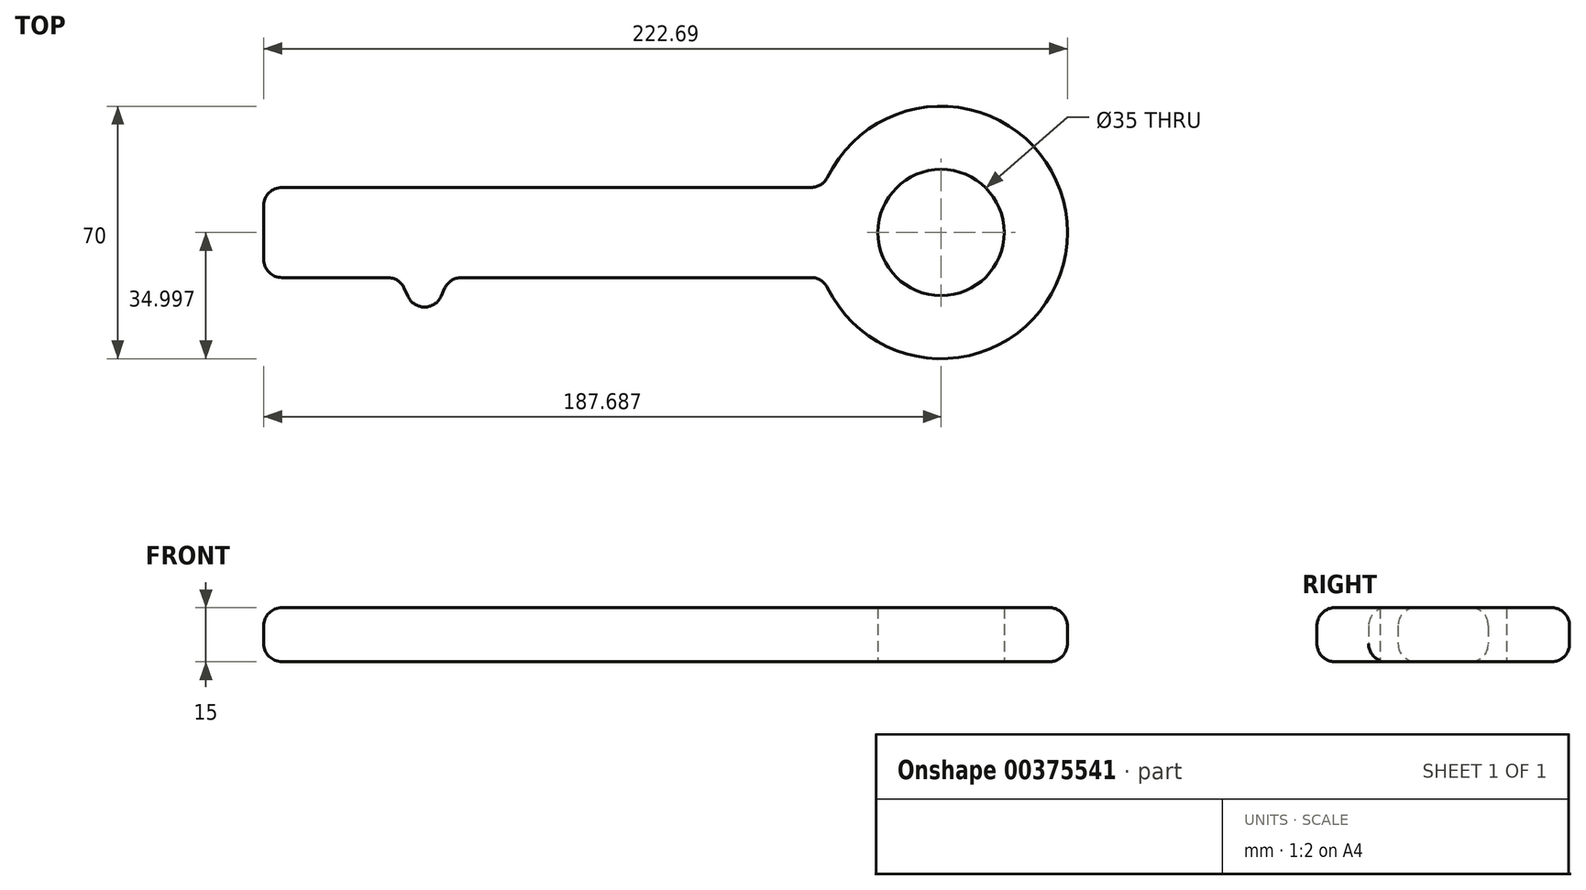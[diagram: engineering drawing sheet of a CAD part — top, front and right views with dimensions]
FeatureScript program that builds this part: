
annotation { "Feature Type Name" : "Feature", "Feature Type Description" : "" }
export const myFeature = defineFeature(function(context is Context, id is Id, definition is map)
    precondition{}
    {
        {
            var Q0;
            Q0=qCreatedBy(makeId("Top.planeOp"),FACE);
            var sketch = newSketch(context, id + "F0", { "sketchPlane" : qUnion([Q0])});
            skLineSegment(sketch, "E0.bottom", {"start": v(-91.14, 51.92) * mm, "end": v(63.86, 51.92) * mm});
            skLineSegment(sketch, "E0.top", {"start": v(-91.14, 26.92) * mm, "end": v(63.86, 26.92) * mm});
            skLineSegment(sketch, "E0.left", {"start": v(-91.14, 51.92) * mm, "end": v(-91.14, 26.92) * mm});
            skLineSegment(sketch, "E0.right", {"start": v(63.86, 51.92) * mm, "end": v(63.86, 26.92) * mm});
            skLineSegment(sketch, "E1.bottom", {"start": v(-91.14, 26.92) * mm, "end": v(-81.14, 26.92) * mm});
            skLineSegment(sketch, "E1.top", {"start": v(-91.14, -3.08) * mm, "end": v(-81.14, -3.08) * mm});
            skLineSegment(sketch, "E1.left", {"start": v(-91.14, 26.92) * mm, "end": v(-91.14, -3.08) * mm});
            skLineSegment(sketch, "E1.right", {"start": v(-81.14, 26.92) * mm, "end": v(-81.14, -3.08) * mm});
            skLineSegment(sketch, "E2.bottom", {"start": v(-71.14, 26.92) * mm, "end": v(-63.6, 26.92) * mm});
            skLineSegment(sketch, "E2.top", {"start": v(-71.14, 11.92) * mm, "end": v(-63.6, 11.92) * mm});
            skLineSegment(sketch, "E2.left", {"start": v(-71.14, 26.92) * mm, "end": v(-71.14, 11.92) * mm});
            skLineSegment(sketch, "E2.right", {"start": v(-63.6, 26.92) * mm, "end": v(-63.6, 11.92) * mm});
            skLineSegment(sketch, "E3", {"start": v(-53.6, 26.92) * mm, "end": v(-46.6, 11.92) * mm});
            skLineSegment(sketch, "E4", {"start": v(-46.6, 11.92) * mm, "end": v(-39.6, 26.92) * mm});
            skLineSegment(sketch, "E5", {"start": v(-39.6, 26.92) * mm, "end": v(-46.6, 26.92) * mm});
            skArc(sketch, "E6", {"start": v(63.86, 26.92) * mm, "mid": v(131.55, 39.42) * mm, "end": v(63.86, 51.92) * mm});
            skCircle(sketch, "E7", {"center": v(96.55, 39.42) * mm, "radius": 17.5 * mm});
            skSolve(sketch);
        }
        {
            var Q0;
            Q0=makeQuery(id+"F0.imprint","IMPRINT",FACE,{"disambiguationData":[TD([[makeQuery(id+"F0.imprint","IMPRINT",EDGE,{"derivedFrom":sQuery(id+"F0.wireOp",EDGE,"E0.bottom")}),-1.0]])]});
            var Q1;
            {var subQ0=sQuery(id+"F0.wireOp",EDGE,"E3");Q1=makeQuery(id+"F0.imprint","IMPRINT",FACE,{"disambiguationData":[TD([[makeQuery(id+"F0.imprint","IMPRINT",EDGE,{"derivedFrom":subQ0}),1.0]])]});}
            var Q2;
            Q2=makeQuery(id+"F0.imprint","IMPRINT",FACE,{"disambiguationData":[TD([[makeQuery(id+"F0.imprint","IMPRINT",EDGE,{"derivedFrom":sQuery(id+"F0.wireOp",EDGE,"E2.bottom")}),-1.0]])]});
            var Q3;
            Q3=makeQuery(id+"F0.imprint","IMPRINT",FACE,{"disambiguationData":[TD([[makeQuery(id+"F0.imprint","IMPRINT",EDGE,{"derivedFrom":sQuery(id+"F0.wireOp",EDGE,"E1.bottom")}),-1.0]])]});
            var Q4;
            Q4=makeQuery(id+"F0.imprint","IMPRINT",FACE,{"disambiguationData":[TD([[makeQuery(id+"F0.imprint","IMPRINT",EDGE,{"derivedFrom":sQuery(id+"F0.wireOp",EDGE,"E0.right")}),1.0]])]});
            extrude(context, id + "F1", {"entities" : qUnion([Q0, Q1, Q2, Q3, Q4]), "depth" : 15 * mm});
        }
        {
            var Q0;
            Q0=makeQuery(id+"F1.opExtrude","CAP_EDGE",EDGE,{"disambiguationData":[OSD([sQuery(id+"F0.wireOp",EDGE,"E0.bottom")])],"isStart":false});
            var Q1;
            Q1=makeQuery(id+"F1.opExtrude","CAP_EDGE",EDGE,{"disambiguationData":[OSD([sQuery(id+"F0.wireOp",EDGE,"E0.left"),sQuery(id+"F0.wireOp",EDGE,"E1.left")])],"isStart":false});
            var Q2;
            Q2=makeQuery(id+"F1.opExtrude","CAP_EDGE",EDGE,{"disambiguationData":[OSD([sQuery(id+"F0.wireOp",EDGE,"E1.right")])],"isStart":false});
            var Q3;
            Q3=makeQuery(id+"F1.opExtrude","CAP_EDGE",EDGE,{"disambiguationData":[OSD([sQuery(id+"F0.wireOp",EDGE,"E1.top")])],"isStart":false});
            var Q4;
            Q4=makeQuery(id+"F1.opExtrude","CAP_EDGE",EDGE,{"disambiguationData":[OSD([sQuery(id+"F0.wireOp",EDGE,"E2.left")])],"isStart":false});
            var Q5;
            {var subQ0=sQuery(id+"F0.wireOp",EDGE,"E0.top");Q5=makeQuery(id+"F1.opExtrude","CAP_EDGE",EDGE,{"disambiguationData":[OSD([subQ0]),TDD([makeQuery(id+"F0.imprint","IMPRINT",EDGE,{"disambiguationData":[TD([[makeQuery(id+"F0.imprint","INTERSECT",VERTEX,{"derivedFrom":[subQ0,sQuery(id+"F0.wireOp",EDGE,"E3")]}),1.0]])],"derivedFrom":subQ0})])],"isStart":false});}
            var Q6;
            Q6=makeQuery(id+"F1.opExtrude","CAP_EDGE",EDGE,{"disambiguationData":[OSD([sQuery(id+"F0.wireOp",EDGE,"E2.right")])],"isStart":false});
            var Q7;
            Q7=makeQuery(id+"F1.opExtrude","CAP_EDGE",EDGE,{"disambiguationData":[OSD([sQuery(id+"F0.wireOp",EDGE,"E3")])],"isStart":false});
            var Q8;
            Q8=makeQuery(id+"F1.opExtrude","CAP_EDGE",EDGE,{"disambiguationData":[OSD([sQuery(id+"F0.wireOp",EDGE,"E2.top")])],"isStart":false});
            var Q9;
            Q9=makeQuery(id+"F1.opExtrude","CAP_EDGE",EDGE,{"disambiguationData":[OSD([sQuery(id+"F0.wireOp",EDGE,"E4")])],"isStart":false});
            var Q10;
            {var subQ0=sQuery(id+"F0.wireOp",EDGE,"E0.top");Q10=makeQuery(id+"F1.opExtrude","CAP_EDGE",EDGE,{"disambiguationData":[OSD([subQ0]),TDD([makeQuery(id+"F0.imprint","IMPRINT",EDGE,{"disambiguationData":[TD([[makeQuery(id+"F0.imprint","INTERSECT",VERTEX,{"derivedFrom":[subQ0,sQuery(id+"F0.wireOp",EDGE,"E0.right"),sQuery(id+"F0.wireOp",EDGE,"E6")]}),1.0]])],"derivedFrom":subQ0})])],"isStart":false});}
            var Q11;
            {var subQ0=sQuery(id+"F0.wireOp",EDGE,"E0.top");Q11=makeQuery(id+"F1.opExtrude","CAP_EDGE",EDGE,{"disambiguationData":[OSD([subQ0]),TDD([makeQuery(id+"F0.imprint","IMPRINT",EDGE,{"disambiguationData":[TD([[makeQuery(id+"F0.imprint","INTERSECT",VERTEX,{"derivedFrom":[subQ0,sQuery(id+"F0.wireOp",EDGE,"E1.bottom"),sQuery(id+"F0.wireOp",EDGE,"E1.right")]}),-1.0]])],"derivedFrom":subQ0})])],"isStart":false});}
            var Q12;
            Q12=makeQuery(id+"F1.opExtrude","CAP_EDGE",EDGE,{"disambiguationData":[OSD([sQuery(id+"F0.wireOp",EDGE,"E0.left"),sQuery(id+"F0.wireOp",EDGE,"E1.left")])],"isStart":true});
            var Q13;
            Q13=makeQuery(id+"F1.opExtrude","SWEPT_EDGE",EDGE,{"disambiguationData":[OSD([sQuery(id+"F0.wireOp",EDGE,"E0.bottom"),sQuery(id+"F0.wireOp",EDGE,"E0.left")])]});
            var Q14;
            Q14=makeQuery(id+"F1.opExtrude","CAP_EDGE",EDGE,{"disambiguationData":[OSD([sQuery(id+"F0.wireOp",EDGE,"E6")])],"isStart":false});
            var Q15;
            Q15=makeQuery(id+"F1.opExtrude","CAP_EDGE",EDGE,{"disambiguationData":[OSD([sQuery(id+"F0.wireOp",EDGE,"E6")])],"isStart":true});
            var Q16;
            Q16=makeQuery(id+"F1.opExtrude","SWEPT_FACE",FACE,{"disambiguationData":[OSD([sQuery(id+"F0.wireOp",EDGE,"E6")])]});
            var Q17;
            Q17=makeQuery(id+"F1.opExtrude","SWEPT_EDGE",EDGE,{"disambiguationData":[OSD([sQuery(id+"F0.wireOp",EDGE,"E1.top"),sQuery(id+"F0.wireOp",EDGE,"E1.left")])]});
            var Q18;
            {var subQ0=sQuery(id+"F0.wireOp",EDGE,"E0.top");Q18=makeQuery(id+"F1.opExtrude","CAP_EDGE",EDGE,{"disambiguationData":[OSD([subQ0]),TDD([makeQuery(id+"F0.imprint","IMPRINT",EDGE,{"disambiguationData":[TD([[makeQuery(id+"F0.imprint","INTERSECT",VERTEX,{"derivedFrom":[subQ0,sQuery(id+"F0.wireOp",EDGE,"E0.right"),sQuery(id+"F0.wireOp",EDGE,"E6")]}),1.0]])],"derivedFrom":subQ0})])],"isStart":true});}
            var Q19;
            Q19=makeQuery(id+"F1.opExtrude","SWEPT_EDGE",EDGE,{"disambiguationData":[OSD([sQuery(id+"F0.wireOp",EDGE,"E3"),sQuery(id+"F0.wireOp",EDGE,"E4")])]});
            var Q20;
            Q20=makeQuery(id+"F1.opExtrude","SWEPT_EDGE",EDGE,{"disambiguationData":[OSD([sQuery(id+"F0.wireOp",EDGE,"E2.top"),sQuery(id+"F0.wireOp",EDGE,"E2.right")])]});
            var Q21;
            Q21=makeQuery(id+"F1.opExtrude","SWEPT_EDGE",EDGE,{"disambiguationData":[OSD([sQuery(id+"F0.wireOp",EDGE,"E0.top"),sQuery(id+"F0.wireOp",EDGE,"E3")])]});
            var Q22;
            Q22=makeQuery(id+"F1.opExtrude","SWEPT_EDGE",EDGE,{"disambiguationData":[OSD([sQuery(id+"F0.wireOp",EDGE,"E0.top"),sQuery(id+"F0.wireOp",EDGE,"E2.bottom"),sQuery(id+"F0.wireOp",EDGE,"E2.left")])]});
            var Q23;
            Q23=makeQuery(id+"F1.opExtrude","SWEPT_EDGE",EDGE,{"disambiguationData":[OSD([sQuery(id+"F0.wireOp",EDGE,"E2.top"),sQuery(id+"F0.wireOp",EDGE,"E2.left")])]});
            var Q24;
            Q24=makeQuery(id+"F1.opExtrude","CAP_EDGE",EDGE,{"disambiguationData":[OSD([sQuery(id+"F0.wireOp",EDGE,"E0.bottom")])],"isStart":true});
            var Q25;
            {var subQ0=sQuery(id+"F0.wireOp",EDGE,"E0.top");Q25=makeQuery(id+"F1.opExtrude","CAP_EDGE",EDGE,{"disambiguationData":[OSD([subQ0]),TDD([makeQuery(id+"F0.imprint","IMPRINT",EDGE,{"disambiguationData":[TD([[makeQuery(id+"F0.imprint","INTERSECT",VERTEX,{"derivedFrom":[subQ0,sQuery(id+"F0.wireOp",EDGE,"E1.bottom"),sQuery(id+"F0.wireOp",EDGE,"E1.right")]}),-1.0]])],"derivedFrom":subQ0})])],"isStart":true});}
            var Q26;
            Q26=makeQuery(id+"F1.opExtrude","CAP_EDGE",EDGE,{"disambiguationData":[OSD([sQuery(id+"F0.wireOp",EDGE,"E1.top")])],"isStart":true});
            var Q27;
            Q27=makeQuery(id+"F1.opExtrude","SWEPT_EDGE",EDGE,{"disambiguationData":[OSD([sQuery(id+"F0.wireOp",EDGE,"E1.top"),sQuery(id+"F0.wireOp",EDGE,"E1.right")])]});
            var Q28;
            Q28=makeQuery(id+"F1.opExtrude","CAP_EDGE",EDGE,{"disambiguationData":[OSD([sQuery(id+"F0.wireOp",EDGE,"E2.top")])],"isStart":true});
            var Q29;
            {var subQ0=sQuery(id+"F0.wireOp",EDGE,"E0.top");Q29=makeQuery(id+"F1.opExtrude","CAP_EDGE",EDGE,{"disambiguationData":[OSD([subQ0]),TDD([makeQuery(id+"F0.imprint","IMPRINT",EDGE,{"disambiguationData":[TD([[makeQuery(id+"F0.imprint","INTERSECT",VERTEX,{"derivedFrom":[subQ0,sQuery(id+"F0.wireOp",EDGE,"E3")]}),1.0]])],"derivedFrom":subQ0})])],"isStart":true});}
            var Q30;
            Q30=makeQuery(id+"F1.opExtrude","CAP_EDGE",EDGE,{"disambiguationData":[OSD([sQuery(id+"F0.wireOp",EDGE,"E3")])],"isStart":true});
            var Q31;
            Q31=makeQuery(id+"F1.opExtrude","CAP_EDGE",EDGE,{"disambiguationData":[OSD([sQuery(id+"F0.wireOp",EDGE,"E4")])],"isStart":true});
            var Q32;
            Q32=makeQuery(id+"F1.opExtrude","SWEPT_EDGE",EDGE,{"disambiguationData":[OSD([sQuery(id+"F0.wireOp",EDGE,"E0.top"),sQuery(id+"F0.wireOp",EDGE,"E4"),sQuery(id+"F0.wireOp",EDGE,"E5")])]});
            fillet(context, id + "F2", {"entities" : qUnion([Q0, Q1, Q2, Q3, Q4, Q5, Q6, Q7, Q8, Q9, Q10, Q11, Q12, Q13, Q14, Q15, Q16, Q17, Q18, Q19, Q20, Q21, Q22, Q23, Q24, Q25, Q26, Q27, Q28, Q29, Q30, Q31, Q32]), "radius" : 5 * mm, "tangentPropagation" : true, "allowEdgeOverflow" : false});
        }
    });
